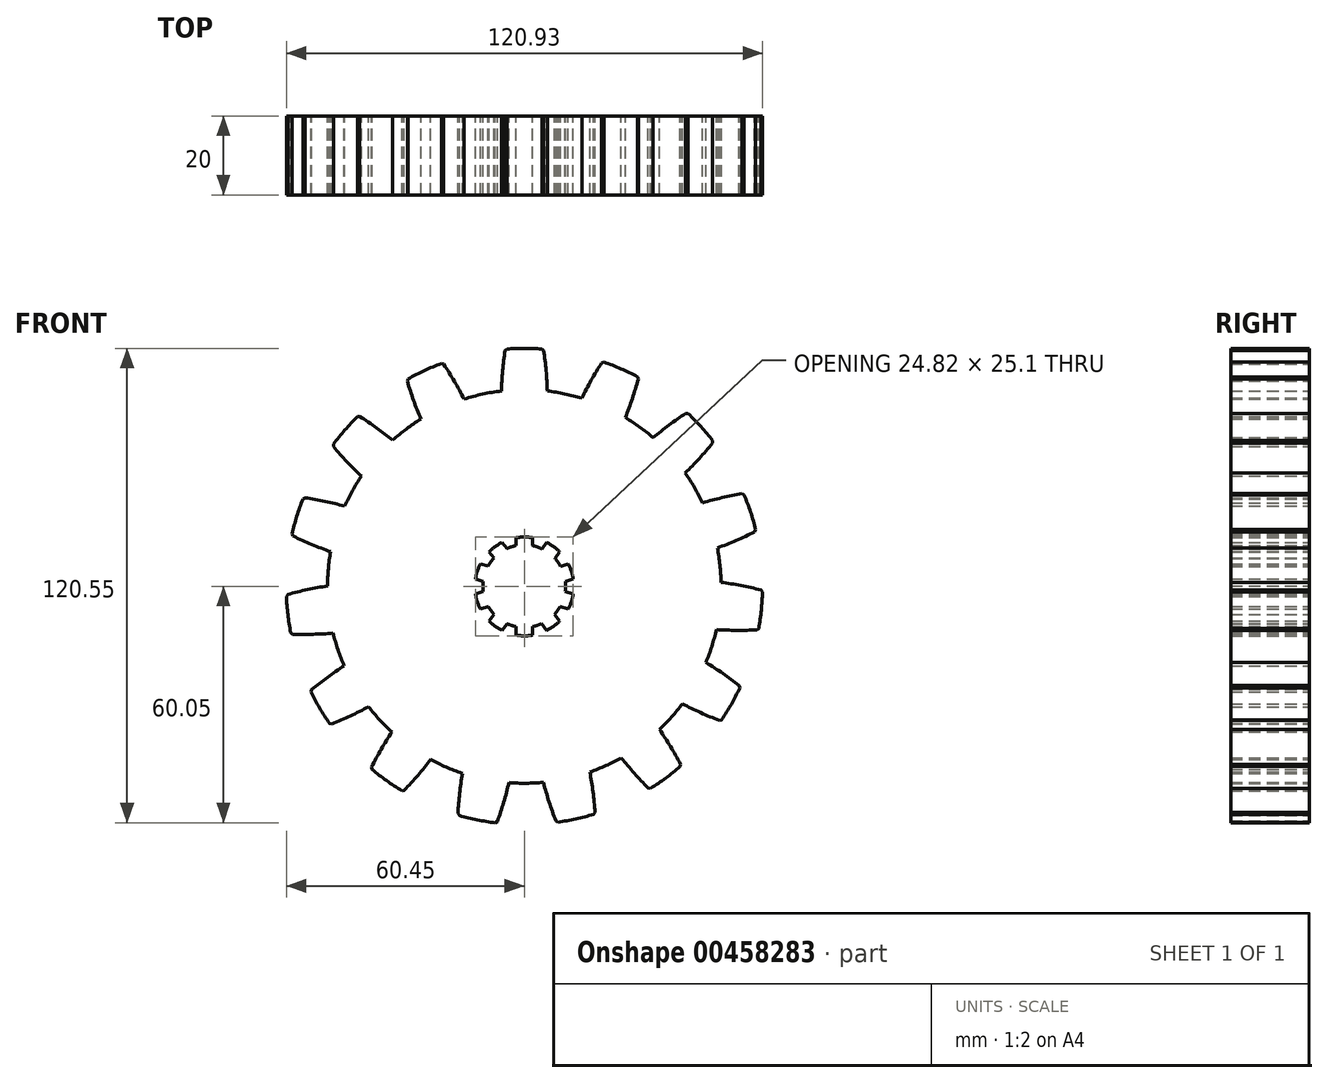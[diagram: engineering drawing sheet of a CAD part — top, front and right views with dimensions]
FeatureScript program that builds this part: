
annotation { "Feature Type Name" : "Feature", "Feature Type Description" : "" }
export const myFeature = defineFeature(function(context is Context, id is Id, definition is map)
    precondition{}
    {
        {
            var Q0;
            Q0=qCreatedBy(makeId("Front.planeOp"),FACE);
            var sketch = newSketch(context, id + "F0", { "sketchPlane" : qUnion([Q0])});
            skLineSegment(sketch, "E0.bottom", {"start": v(-2.05, 0) * mm, "end": v(2.05, 0) * mm});
            skLineSegment(sketch, "E0.left", {"start": v(-2.05, 0) * mm, "end": v(-2.05, 12.38) * mm});
            skLineSegment(sketch, "E0.right", {"start": v(2.05, 0) * mm, "end": v(2.05, 12.38) * mm});
            skArc(sketch, "E1", {"start": v(-5.62, 11.22) * mm, "mid": v(-7.38, 10.15) * mm, "end": v(-8.94, 8.81) * mm});
            skPoint(sketch, "E2", {"position": v(2.05, 12.38) * mm});
            skPoint(sketch, "E3", {"position": v(-2.05, 12.38) * mm});
            skLineSegment(sketch, "E4", {"start": v(-2.06, 12.38) * mm, "end": v(-2.05, 12.38) * mm, "construction": true});
            skLineSegment(sketch, "E5.1.0", {"start": v(1.66, 1.2) * mm, "end": v(-5.62, 11.22) * mm});
            skLineSegment(sketch, "E5.1.1", {"start": v(-1.66, -1.2) * mm, "end": v(-8.94, 8.81) * mm});
            skLineSegment(sketch, "E5.1.2", {"start": v(-1.66, -1.2) * mm, "end": v(1.66, 1.2) * mm});
            skLineSegment(sketch, "E5.2.0", {"start": v(0.63, 1.95) * mm, "end": v(-11.14, 5.78) * mm});
            skLineSegment(sketch, "E5.2.1", {"start": v(-0.63, -1.95) * mm, "end": v(-12.4, 1.88) * mm});
            skLineSegment(sketch, "E5.2.2", {"start": v(-0.63, -1.95) * mm, "end": v(0.63, 1.95) * mm});
            skLineSegment(sketch, "E5.3.0", {"start": v(-0.63, 1.95) * mm, "end": v(-12.4, -1.88) * mm});
            skLineSegment(sketch, "E5.3.1", {"start": v(0.63, -1.95) * mm, "end": v(-11.14, -5.78) * mm});
            skLineSegment(sketch, "E5.3.2", {"start": v(0.63, -1.95) * mm, "end": v(-0.63, 1.95) * mm});
            skLineSegment(sketch, "E5.4.0", {"start": v(-1.66, 1.2) * mm, "end": v(-8.94, -8.81) * mm});
            skLineSegment(sketch, "E5.4.1", {"start": v(1.66, -1.2) * mm, "end": v(-5.62, -11.22) * mm});
            skLineSegment(sketch, "E5.4.2", {"start": v(1.66, -1.2) * mm, "end": v(-1.66, 1.2) * mm});
            skLineSegment(sketch, "E5.5.0", {"start": v(-2.05, 0) * mm, "end": v(-2.05, -12.38) * mm});
            skLineSegment(sketch, "E5.5.1", {"start": v(2.05, 0) * mm, "end": v(2.05, -12.38) * mm});
            skLineSegment(sketch, "E5.5.2", {"start": v(2.05, 0) * mm, "end": v(-2.05, 0) * mm});
            skLineSegment(sketch, "E5.6.0", {"start": v(-1.66, -1.2) * mm, "end": v(5.62, -11.22) * mm});
            skLineSegment(sketch, "E5.6.1", {"start": v(1.66, 1.2) * mm, "end": v(8.94, -8.81) * mm});
            skLineSegment(sketch, "E5.6.2", {"start": v(1.66, 1.2) * mm, "end": v(-1.66, -1.2) * mm});
            skLineSegment(sketch, "E5.7.0", {"start": v(-0.63, -1.95) * mm, "end": v(11.14, -5.78) * mm});
            skLineSegment(sketch, "E5.7.1", {"start": v(0.63, 1.95) * mm, "end": v(12.4, -1.88) * mm});
            skLineSegment(sketch, "E5.7.2", {"start": v(0.63, 1.95) * mm, "end": v(-0.63, -1.95) * mm});
            skLineSegment(sketch, "E5.8.0", {"start": v(0.63, -1.95) * mm, "end": v(12.4, 1.88) * mm});
            skLineSegment(sketch, "E5.8.1", {"start": v(-0.63, 1.95) * mm, "end": v(11.14, 5.78) * mm});
            skLineSegment(sketch, "E5.8.2", {"start": v(-0.63, 1.95) * mm, "end": v(0.63, -1.95) * mm});
            skLineSegment(sketch, "E5.9.0", {"start": v(1.66, -1.2) * mm, "end": v(8.94, 8.81) * mm});
            skLineSegment(sketch, "E5.9.1", {"start": v(-1.66, 1.2) * mm, "end": v(5.62, 11.22) * mm});
            skLineSegment(sketch, "E5.9.2", {"start": v(-1.66, 1.2) * mm, "end": v(1.66, -1.2) * mm});
            skArc(sketch, "E6.trimOffspring", {"start": v(-11.14, 5.78) * mm, "mid": v(-11.94, 3.88) * mm, "end": v(-12.4, 1.88) * mm});
            skArc(sketch, "E7.trimOffspring", {"start": v(-12.4, -1.88) * mm, "mid": v(-11.94, -3.88) * mm, "end": v(-11.14, -5.78) * mm});
            skArc(sketch, "E8.trimOffspring", {"start": v(-8.94, -8.81) * mm, "mid": v(-7.38, -10.15) * mm, "end": v(-5.62, -11.22) * mm});
            skArc(sketch, "E9.trimOffspring", {"start": v(-2.05, -12.38) * mm, "mid": v(0, -12.55) * mm, "end": v(2.05, -12.38) * mm});
            skArc(sketch, "E10.trimOffspring", {"start": v(5.62, -11.22) * mm, "mid": v(7.38, -10.15) * mm, "end": v(8.94, -8.81) * mm});
            skArc(sketch, "E11.trimOffspring", {"start": v(11.14, -5.78) * mm, "mid": v(11.94, -3.88) * mm, "end": v(12.4, -1.88) * mm});
            skArc(sketch, "E12.trimOffspring", {"start": v(12.4, 1.88) * mm, "mid": v(11.94, 3.88) * mm, "end": v(11.14, 5.78) * mm});
            skArc(sketch, "E13.trimOffspring", {"start": v(8.94, 8.81) * mm, "mid": v(7.38, 10.15) * mm, "end": v(5.62, 11.22) * mm});
            skArc(sketch, "E14.trimOffspring", {"start": v(2.05, 12.38) * mm, "mid": v(0, 12.55) * mm, "end": v(-2.06, 12.38) * mm});
            skCircle(sketch, "E15", {"center": v(-0.03, 0.08) * mm, "radius": 10.5 * mm});
            skSolve(sketch);
        }
        {
            var Q0;
            Q0=qCreatedBy(makeId("Front.planeOp"),FACE);
            var sketch = newSketch(context, id + "F1", { "sketchPlane" : qUnion([Q0])});
            skCircle(sketch, "E16", {"center": v(0, 0) * mm, "radius": 50 * mm});
            skLineSegment(sketch, "E17", {"start": v(0, 50) * mm, "end": v(-29, 50) * mm, "construction": true});
            skLineSegment(sketch, "E18", {"start": v(-29, 50) * mm, "end": v(-29, 46.5) * mm, "construction": true});
            skLineSegment(sketch, "E19", {"start": v(-29, 46.5) * mm, "end": v(0, 46.5) * mm, "construction": true});
            skLineSegment(sketch, "E20", {"start": v(0, 46.5) * mm, "end": v(84.1, 46.5) * mm, "construction": true});
            skArc(sketch, "E21", {"start": v(-4.83, 60.3) * mm, "mid": v(-5.5, 55) * mm, "end": v(-5.84, 49.66) * mm});
            skArc(sketch, "E22.MirrorC", {"start": v(4.83, 60.3) * mm, "mid": v(5.5, 55) * mm, "end": v(5.84, 49.66) * mm});
            skArc(sketch, "E23", {"start": v(4.83, 60.3) * mm, "mid": v(0, 60.5) * mm, "end": v(-4.83, 60.3) * mm});
            skArc(sketch, "E24.1.0", {"start": v(29.06, 53.07) * mm, "mid": v(24.54, 55.3) * mm, "end": v(19.85, 57.15) * mm});
            skArc(sketch, "E24.1.1", {"start": v(29.06, 53.07) * mm, "mid": v(27.5, 47.94) * mm, "end": v(25.66, 42.92) * mm});
            skArc(sketch, "E24.1.2", {"start": v(19.85, 57.15) * mm, "mid": v(17.09, 52.56) * mm, "end": v(14.6, 47.82) * mm});
            skArc(sketch, "E24.2.0", {"start": v(48.08, 36.72) * mm, "mid": v(44.86, 40.6) * mm, "end": v(41.32, 44.19) * mm});
            skArc(sketch, "E24.2.1", {"start": v(48.08, 36.72) * mm, "mid": v(44.59, 32.66) * mm, "end": v(40.86, 28.82) * mm});
            skArc(sketch, "E24.2.2", {"start": v(41.32, 44.19) * mm, "mid": v(36.94, 41.11) * mm, "end": v(32.75, 37.79) * mm});
            skArc(sketch, "E24.3.0", {"start": v(58.84, 14.06) * mm, "mid": v(57.47, 18.91) * mm, "end": v(55.7, 23.63) * mm});
            skArc(sketch, "E24.3.1", {"start": v(58.84, 14.06) * mm, "mid": v(54, 11.77) * mm, "end": v(49.04, 9.77) * mm});
            skArc(sketch, "E24.3.2", {"start": v(55.7, 23.63) * mm, "mid": v(50.44, 22.6) * mm, "end": v(45.26, 21.26) * mm});
            skArc(sketch, "E24.4.0", {"start": v(59.49, -11.02) * mm, "mid": v(60.2, -6.02) * mm, "end": v(60.5, -1) * mm});
            skArc(sketch, "E24.4.1", {"start": v(59.49, -11.02) * mm, "mid": v(54.14, -11.15) * mm, "end": v(48.78, -10.96) * mm});
            skArc(sketch, "E24.4.2", {"start": v(60.5, -1) * mm, "mid": v(55.27, 0.2) * mm, "end": v(49.99, 1.07) * mm});
            skArc(sketch, "E24.5.0", {"start": v(49.9, -34.2) * mm, "mid": v(52.58, -29.92) * mm, "end": v(54.9, -25.44) * mm});
            skArc(sketch, "E24.5.1", {"start": v(49.9, -34.2) * mm, "mid": v(44.96, -32.14) * mm, "end": v(40.15, -29.8) * mm});
            skArc(sketch, "E24.5.2", {"start": v(54.9, -25.44) * mm, "mid": v(50.6, -22.24) * mm, "end": v(46.13, -19.3) * mm});
            skArc(sketch, "E24.6.0", {"start": v(31.75, -51.5) * mm, "mid": v(35.93, -48.68) * mm, "end": v(39.85, -45.52) * mm});
            skArc(sketch, "E24.6.1", {"start": v(31.75, -51.5) * mm, "mid": v(28.06, -47.62) * mm, "end": v(24.6, -43.52) * mm});
            skArc(sketch, "E24.6.2", {"start": v(39.85, -45.52) * mm, "mid": v(37.23, -40.85) * mm, "end": v(34.34, -36.34) * mm});
            skArc(sketch, "E24.7.0", {"start": v(8.13, -59.95) * mm, "mid": v(13.1, -59.07) * mm, "end": v(17.97, -57.77) * mm});
            skArc(sketch, "E24.7.1", {"start": v(8.13, -59.95) * mm, "mid": v(6.33, -54.9) * mm, "end": v(4.84, -49.77) * mm});
            skArc(sketch, "E24.7.2", {"start": v(17.97, -57.77) * mm, "mid": v(17.46, -52.44) * mm, "end": v(16.64, -47.15) * mm});
            skArc(sketch, "E24.8.0", {"start": v(-16.88, -58.1) * mm, "mid": v(-11.99, -59.3) * mm, "end": v(-7, -60.1) * mm});
            skArc(sketch, "E24.8.1", {"start": v(-16.88, -58.1) * mm, "mid": v(-16.48, -52.76) * mm, "end": v(-15.76, -47.45) * mm});
            skArc(sketch, "E24.8.2", {"start": v(-7, -60.1) * mm, "mid": v(-5.3, -55.02) * mm, "end": v(-3.9, -49.85) * mm});
            skArc(sketch, "E24.9.0", {"start": v(-39, -46.26) * mm, "mid": v(-35, -49.34) * mm, "end": v(-30.78, -52.09) * mm});
            skArc(sketch, "E24.9.1", {"start": v(-39, -46.26) * mm, "mid": v(-36.46, -41.54) * mm, "end": v(-33.65, -36.98) * mm});
            skArc(sketch, "E24.9.2", {"start": v(-30.78, -52.09) * mm, "mid": v(-27.16, -48.14) * mm, "end": v(-23.8, -43.98) * mm});
            skArc(sketch, "E24.10.0", {"start": v(-54.4, -26.46) * mm, "mid": v(-52.01, -30.9) * mm, "end": v(-49.26, -35.12) * mm});
            skArc(sketch, "E24.10.1", {"start": v(-54.4, -26.46) * mm, "mid": v(-50.18, -23.18) * mm, "end": v(-45.76, -20.15) * mm});
            skArc(sketch, "E24.10.2", {"start": v(-49.26, -35.12) * mm, "mid": v(-44.35, -32.98) * mm, "end": v(-39.58, -30.55) * mm});
            skArc(sketch, "E24.11.0", {"start": v(-60.46, -2.12) * mm, "mid": v(-60.08, -7.15) * mm, "end": v(-59.27, -12.13) * mm});
            skArc(sketch, "E24.11.1", {"start": v(-60.46, -2.12) * mm, "mid": v(-55.26, -0.84) * mm, "end": v(-50, 0.14) * mm});
            skArc(sketch, "E24.11.2", {"start": v(-59.27, -12.13) * mm, "mid": v(-53.92, -12.16) * mm, "end": v(-48.57, -11.87) * mm});
            skArc(sketch, "E24.12.0", {"start": v(-56.13, 22.58) * mm, "mid": v(-57.81, 17.83) * mm, "end": v(-59.1, 12.96) * mm});
            skArc(sketch, "E24.12.1", {"start": v(-56.13, 22.58) * mm, "mid": v(-50.85, 21.65) * mm, "end": v(-45.65, 20.4) * mm});
            skArc(sketch, "E24.12.2", {"start": v(-59.1, 12.96) * mm, "mid": v(-54.21, 10.76) * mm, "end": v(-49.21, 8.85) * mm});
            skArc(sketch, "E24.13.0", {"start": v(-42.14, 43.4) * mm, "mid": v(-45.61, 39.75) * mm, "end": v(-48.76, 35.81) * mm});
            skArc(sketch, "E24.13.1", {"start": v(-42.14, 43.4) * mm, "mid": v(-37.7, 40.42) * mm, "end": v(-33.45, 37.17) * mm});
            skArc(sketch, "E24.13.2", {"start": v(-48.76, 35.81) * mm, "mid": v(-45.2, 31.82) * mm, "end": v(-41.39, 28.05) * mm});
            skArc(sketch, "E24.14.0", {"start": v(-20.71, 56.79) * mm, "mid": v(-25.37, 54.85) * mm, "end": v(-29.84, 52.53) * mm});
            skArc(sketch, "E24.14.1", {"start": v(-20.71, 56.79) * mm, "mid": v(-17.87, 52.25) * mm, "end": v(-15.3, 47.55) * mm});
            skArc(sketch, "E24.14.2", {"start": v(-29.84, 52.53) * mm, "mid": v(-28.2, 47.43) * mm, "end": v(-26.25, 42.44) * mm});
            skPoint(sketch, "E24.center", {"position": v(0.2, 0.02) * mm});
            skLineSegment(sketch, "E24.anchor1", {"start": v(0.2, 0.02) * mm, "end": v(-4.83, 60.3) * mm, "construction": true});
            skLineSegment(sketch, "E24.anchor2", {"start": v(0.2, 0.02) * mm, "end": v(-29.84, 52.53) * mm, "construction": true});
            skSolve(sketch);
        }
        {
            var Q0;
            Q0 = qSketchRegion(id + "F1", true);
            extrude(context, id + "F2", {"entities" : qUnion([Q0]), "depth" : 20 * mm, "offsetDistance" : 25 * mm});
        }
        {
            var Q0;
            Q0 = qSketchRegion(id + "F0", true);
            var Q1;
            Q1=makeQuery(id+"F2.opExtrude","CAP_FACE",FACE,{"disambiguationData":[OSD([sQuery(id+"F1.wireOp",EDGE,"E16"),sQuery(id+"F1.wireOp",EDGE,"E21"),sQuery(id+"F1.wireOp",EDGE,"E22.MirrorC"),sQuery(id+"F1.wireOp",EDGE,"E23"),sQuery(id+"F1.wireOp",EDGE,"E24.1.0"),sQuery(id+"F1.wireOp",EDGE,"E24.1.1"),sQuery(id+"F1.wireOp",EDGE,"E24.1.2"),sQuery(id+"F1.wireOp",EDGE,"E24.2.0"),sQuery(id+"F1.wireOp",EDGE,"E24.2.1"),sQuery(id+"F1.wireOp",EDGE,"E24.2.2"),sQuery(id+"F1.wireOp",EDGE,"E24.3.0"),sQuery(id+"F1.wireOp",EDGE,"E24.3.1"),sQuery(id+"F1.wireOp",EDGE,"E24.3.2"),sQuery(id+"F1.wireOp",EDGE,"E24.4.0"),sQuery(id+"F1.wireOp",EDGE,"E24.4.1"),sQuery(id+"F1.wireOp",EDGE,"E24.4.2"),sQuery(id+"F1.wireOp",EDGE,"E24.5.0"),sQuery(id+"F1.wireOp",EDGE,"E24.5.1"),sQuery(id+"F1.wireOp",EDGE,"E24.5.2"),sQuery(id+"F1.wireOp",EDGE,"E24.6.0"),sQuery(id+"F1.wireOp",EDGE,"E24.6.1"),sQuery(id+"F1.wireOp",EDGE,"E24.6.2"),sQuery(id+"F1.wireOp",EDGE,"E24.7.0"),sQuery(id+"F1.wireOp",EDGE,"E24.7.1"),sQuery(id+"F1.wireOp",EDGE,"E24.7.2"),sQuery(id+"F1.wireOp",EDGE,"E24.8.0"),sQuery(id+"F1.wireOp",EDGE,"E24.8.1"),sQuery(id+"F1.wireOp",EDGE,"E24.8.2"),sQuery(id+"F1.wireOp",EDGE,"E24.9.0"),sQuery(id+"F1.wireOp",EDGE,"E24.9.1"),sQuery(id+"F1.wireOp",EDGE,"E24.9.2"),sQuery(id+"F1.wireOp",EDGE,"E24.10.0"),sQuery(id+"F1.wireOp",EDGE,"E24.10.1"),sQuery(id+"F1.wireOp",EDGE,"E24.10.2"),sQuery(id+"F1.wireOp",EDGE,"E24.11.0"),sQuery(id+"F1.wireOp",EDGE,"E24.11.1"),sQuery(id+"F1.wireOp",EDGE,"E24.11.2"),sQuery(id+"F1.wireOp",EDGE,"E24.12.0"),sQuery(id+"F1.wireOp",EDGE,"E24.12.1"),sQuery(id+"F1.wireOp",EDGE,"E24.12.2"),sQuery(id+"F1.wireOp",EDGE,"E24.13.0"),sQuery(id+"F1.wireOp",EDGE,"E24.13.1"),sQuery(id+"F1.wireOp",EDGE,"E24.13.2"),sQuery(id+"F1.wireOp",EDGE,"E24.14.0"),sQuery(id+"F1.wireOp",EDGE,"E24.14.1"),sQuery(id+"F1.wireOp",EDGE,"E24.14.2")])],"isStart":false});
            extrude(context, id + "F3", {"entities" : qUnion([Q0]), "operationType" : NewBodyOperationType.REMOVE, "endBound" : BoundingType.UP_TO_SURFACE, "endBoundEntityFace" : qUnion([Q1]), "depth" : 25 * mm});
        }
        {
            var Q0;
            {var subQ13=sQuery(id+"F0.wireOp",EDGE,"E5.2.0");var subQ14=sQuery(id+"F0.wireOp",EDGE,"E0.left");var subQ15=makeQuery(id+"F0.imprint","INTERSECT",VERTEX,{"derivedFrom":[subQ14,subQ13]});Q0=makeQuery(id+"F3.boolean.opBoolean","SPLIT",FACE,{"disambiguationData":[TD([makeQuery(id+"F3.opExtrude","SWEPT_FACE",FACE,{"disambiguationData":[OSD([subQ14]),TDD([makeQuery(id+"F0.imprint","IMPRINT",EDGE,{"disambiguationData":[TD([[subQ15,-1.0]])],"derivedFrom":subQ14})])]})])],"derivedFrom":makeQuery(id+"F2.opExtrude","CAP_FACE",FACE,{"disambiguationData":[OSD([sQuery(id+"F1.wireOp",EDGE,"E16"),sQuery(id+"F1.wireOp",EDGE,"E21"),sQuery(id+"F1.wireOp",EDGE,"E22.MirrorC"),sQuery(id+"F1.wireOp",EDGE,"E23"),sQuery(id+"F1.wireOp",EDGE,"E24.1.0"),sQuery(id+"F1.wireOp",EDGE,"E24.1.1"),sQuery(id+"F1.wireOp",EDGE,"E24.1.2"),sQuery(id+"F1.wireOp",EDGE,"E24.2.0"),sQuery(id+"F1.wireOp",EDGE,"E24.2.1"),sQuery(id+"F1.wireOp",EDGE,"E24.2.2"),sQuery(id+"F1.wireOp",EDGE,"E24.3.0"),sQuery(id+"F1.wireOp",EDGE,"E24.3.1"),sQuery(id+"F1.wireOp",EDGE,"E24.3.2"),sQuery(id+"F1.wireOp",EDGE,"E24.4.0"),sQuery(id+"F1.wireOp",EDGE,"E24.4.1"),sQuery(id+"F1.wireOp",EDGE,"E24.4.2"),sQuery(id+"F1.wireOp",EDGE,"E24.5.0"),sQuery(id+"F1.wireOp",EDGE,"E24.5.1"),sQuery(id+"F1.wireOp",EDGE,"E24.5.2"),sQuery(id+"F1.wireOp",EDGE,"E24.6.0"),sQuery(id+"F1.wireOp",EDGE,"E24.6.1"),sQuery(id+"F1.wireOp",EDGE,"E24.6.2"),sQuery(id+"F1.wireOp",EDGE,"E24.7.0"),sQuery(id+"F1.wireOp",EDGE,"E24.7.1"),sQuery(id+"F1.wireOp",EDGE,"E24.7.2"),sQuery(id+"F1.wireOp",EDGE,"E24.8.0"),sQuery(id+"F1.wireOp",EDGE,"E24.8.1"),sQuery(id+"F1.wireOp",EDGE,"E24.8.2"),sQuery(id+"F1.wireOp",EDGE,"E24.9.0"),sQuery(id+"F1.wireOp",EDGE,"E24.9.1"),sQuery(id+"F1.wireOp",EDGE,"E24.9.2"),sQuery(id+"F1.wireOp",EDGE,"E24.10.0"),sQuery(id+"F1.wireOp",EDGE,"E24.10.1"),sQuery(id+"F1.wireOp",EDGE,"E24.10.2"),sQuery(id+"F1.wireOp",EDGE,"E24.11.0"),sQuery(id+"F1.wireOp",EDGE,"E24.11.1"),sQuery(id+"F1.wireOp",EDGE,"E24.11.2"),sQuery(id+"F1.wireOp",EDGE,"E24.12.0"),sQuery(id+"F1.wireOp",EDGE,"E24.12.1"),sQuery(id+"F1.wireOp",EDGE,"E24.12.2"),sQuery(id+"F1.wireOp",EDGE,"E24.13.0"),sQuery(id+"F1.wireOp",EDGE,"E24.13.1"),sQuery(id+"F1.wireOp",EDGE,"E24.13.2"),sQuery(id+"F1.wireOp",EDGE,"E24.14.0"),sQuery(id+"F1.wireOp",EDGE,"E24.14.1"),sQuery(id+"F1.wireOp",EDGE,"E24.14.2")])],"isStart":false})});}
            var Q1;
            {var subQ9=sQuery(id+"F1.wireOp",EDGE,"E24.14.2");var subQ18=sQuery(id+"F1.wireOp",EDGE,"E24.14.1");var subQ27=sQuery(id+"F1.wireOp",EDGE,"E24.14.0");var subQ29=sQuery(id+"F1.wireOp",EDGE,"E24.13.2");var subQ31=sQuery(id+"F1.wireOp",EDGE,"E24.13.1");var subQ33=sQuery(id+"F1.wireOp",EDGE,"E24.13.0");var subQ35=sQuery(id+"F1.wireOp",EDGE,"E24.12.2");var subQ37=sQuery(id+"F1.wireOp",EDGE,"E24.12.1");var subQ39=sQuery(id+"F1.wireOp",EDGE,"E24.12.0");var subQ41=sQuery(id+"F1.wireOp",EDGE,"E24.11.2");var subQ43=sQuery(id+"F1.wireOp",EDGE,"E24.11.1");var subQ45=sQuery(id+"F1.wireOp",EDGE,"E24.11.0");var subQ46=sQuery(id+"F1.wireOp",EDGE,"E24.10.2");var subQ47=sQuery(id+"F1.wireOp",EDGE,"E24.10.1");var subQ48=sQuery(id+"F1.wireOp",EDGE,"E24.1.2");var subQ49=sQuery(id+"F1.wireOp",EDGE,"E24.2.1");var subQ50=sQuery(id+"F1.wireOp",EDGE,"E24.1.1");var subQ51=sQuery(id+"F1.wireOp",EDGE,"E24.1.0");var subQ52=sQuery(id+"F1.wireOp",EDGE,"E23");var subQ53=sQuery(id+"F1.wireOp",EDGE,"E22.MirrorC");var subQ55=sQuery(id+"F1.wireOp",EDGE,"E21");var subQ56=sQuery(id+"F1.wireOp",EDGE,"E24.4.1");var subQ57=sQuery(id+"F1.wireOp",EDGE,"E16");var subQ58=sQuery(id+"F1.wireOp",EDGE,"E24.5.2");var subQ59=sQuery(id+"F1.wireOp",EDGE,"E24.5.1");var subQ60=sQuery(id+"F1.wireOp",EDGE,"E24.6.2");var subQ61=sQuery(id+"F1.wireOp",EDGE,"E24.6.1");var subQ62=sQuery(id+"F1.wireOp",EDGE,"E24.7.2");var subQ63=sQuery(id+"F1.wireOp",EDGE,"E24.7.1");var subQ64=sQuery(id+"F1.wireOp",EDGE,"E24.8.2");var subQ65=sQuery(id+"F1.wireOp",EDGE,"E24.8.1");var subQ66=sQuery(id+"F1.wireOp",EDGE,"E24.9.2");var subQ67=sQuery(id+"F1.wireOp",EDGE,"E24.2.2");var subQ68=sQuery(id+"F1.wireOp",EDGE,"E24.3.2");var subQ69=sQuery(id+"F1.wireOp",EDGE,"E24.3.0");var subQ70=sQuery(id+"F1.wireOp",EDGE,"E24.2.0");var subQ71=sQuery(id+"F1.wireOp",EDGE,"E24.3.1");var subQ72=sQuery(id+"F1.wireOp",EDGE,"E24.4.2");var subQ73=sQuery(id+"F1.wireOp",EDGE,"E24.10.0");var subQ74=sQuery(id+"F1.wireOp",EDGE,"E24.9.1");var subQ79=sQuery(id+"F1.wireOp",EDGE,"E24.5.0");var subQ80=sQuery(id+"F1.wireOp",EDGE,"E24.4.0");var subQ87=sQuery(id+"F1.wireOp",EDGE,"E24.7.0");var subQ88=sQuery(id+"F1.wireOp",EDGE,"E24.6.0");var subQ95=sQuery(id+"F1.wireOp",EDGE,"E24.9.0");var subQ96=sQuery(id+"F1.wireOp",EDGE,"E24.8.0");Q1=makeQuery(id+"F3.boolean.opBoolean","SPLIT",FACE,{"disambiguationData":[TD([makeQuery(id+"F2.opExtrude","SWEPT_FACE",FACE,{"disambiguationData":[OSD([subQ55])]})])],"derivedFrom":makeQuery(id+"F2.opExtrude","CAP_FACE",FACE,{"disambiguationData":[OSD([subQ57,subQ55,subQ53,subQ52,subQ51,subQ50,subQ48,subQ70,subQ49,subQ67,subQ69,subQ71,subQ68,subQ80,subQ56,subQ72,subQ79,subQ59,subQ58,subQ88,subQ61,subQ60,subQ87,subQ63,subQ62,subQ96,subQ65,subQ64,subQ95,subQ74,subQ66,subQ73,subQ47,subQ46,subQ45,subQ43,subQ41,subQ39,subQ37,subQ35,subQ33,subQ31,subQ29,subQ27,subQ18,subQ9])],"isStart":true})});}
            extrude(context, id + "F4", {"entities" : qUnion([Q0]), "operationType" : NewBodyOperationType.REMOVE, "oppositeDirection" : true, "endBoundEntityFace" : qUnion([Q1]), "depth" : 20 * mm});
        }
        {
            var Q0;
            Q0=makeQuery(id+"F2.opExtrude","SWEPT_EDGE",EDGE,{"disambiguationData":[OSD([sQuery(id+"F1.wireOp",EDGE,"E24.14.0"),sQuery(id+"F1.wireOp",EDGE,"E24.14.2")])]});
            var Q1;
            Q1=makeQuery(id+"F2.opExtrude","SWEPT_EDGE",EDGE,{"disambiguationData":[OSD([sQuery(id+"F1.wireOp",EDGE,"E24.14.0"),sQuery(id+"F1.wireOp",EDGE,"E24.14.1")])]});
            var Q2;
            Q2=makeQuery(id+"F2.opExtrude","SWEPT_EDGE",EDGE,{"disambiguationData":[OSD([sQuery(id+"F1.wireOp",EDGE,"E21"),sQuery(id+"F1.wireOp",EDGE,"E23")])]});
            var Q3;
            Q3=makeQuery(id+"F2.opExtrude","SWEPT_EDGE",EDGE,{"disambiguationData":[OSD([sQuery(id+"F1.wireOp",EDGE,"E22.MirrorC"),sQuery(id+"F1.wireOp",EDGE,"E23")])]});
            var Q4;
            Q4=makeQuery(id+"F2.opExtrude","SWEPT_EDGE",EDGE,{"disambiguationData":[OSD([sQuery(id+"F1.wireOp",EDGE,"E24.1.0"),sQuery(id+"F1.wireOp",EDGE,"E24.1.2")])]});
            var Q5;
            Q5=makeQuery(id+"F2.opExtrude","SWEPT_EDGE",EDGE,{"disambiguationData":[OSD([sQuery(id+"F1.wireOp",EDGE,"E24.1.0"),sQuery(id+"F1.wireOp",EDGE,"E24.1.1")])]});
            var Q6;
            Q6=makeQuery(id+"F2.opExtrude","SWEPT_EDGE",EDGE,{"disambiguationData":[OSD([sQuery(id+"F1.wireOp",EDGE,"E24.2.0"),sQuery(id+"F1.wireOp",EDGE,"E24.2.2")])]});
            var Q7;
            Q7=makeQuery(id+"F2.opExtrude","SWEPT_EDGE",EDGE,{"disambiguationData":[OSD([sQuery(id+"F1.wireOp",EDGE,"E24.2.0"),sQuery(id+"F1.wireOp",EDGE,"E24.2.1")])]});
            var Q8;
            Q8=makeQuery(id+"F2.opExtrude","SWEPT_EDGE",EDGE,{"disambiguationData":[OSD([sQuery(id+"F1.wireOp",EDGE,"E24.3.0"),sQuery(id+"F1.wireOp",EDGE,"E24.3.2")])]});
            var Q9;
            Q9=makeQuery(id+"F2.opExtrude","SWEPT_EDGE",EDGE,{"disambiguationData":[OSD([sQuery(id+"F1.wireOp",EDGE,"E24.3.0"),sQuery(id+"F1.wireOp",EDGE,"E24.3.1")])]});
            var Q10;
            Q10=makeQuery(id+"F2.opExtrude","SWEPT_EDGE",EDGE,{"disambiguationData":[OSD([sQuery(id+"F1.wireOp",EDGE,"E24.4.0"),sQuery(id+"F1.wireOp",EDGE,"E24.4.2")])]});
            var Q11;
            Q11=makeQuery(id+"F2.opExtrude","SWEPT_EDGE",EDGE,{"disambiguationData":[OSD([sQuery(id+"F1.wireOp",EDGE,"E24.4.0"),sQuery(id+"F1.wireOp",EDGE,"E24.4.1")])]});
            var Q12;
            Q12=makeQuery(id+"F2.opExtrude","SWEPT_EDGE",EDGE,{"disambiguationData":[OSD([sQuery(id+"F1.wireOp",EDGE,"E24.5.0"),sQuery(id+"F1.wireOp",EDGE,"E24.5.2")])]});
            var Q13;
            Q13=makeQuery(id+"F2.opExtrude","SWEPT_EDGE",EDGE,{"disambiguationData":[OSD([sQuery(id+"F1.wireOp",EDGE,"E24.5.0"),sQuery(id+"F1.wireOp",EDGE,"E24.5.1")])]});
            var Q14;
            Q14=makeQuery(id+"F2.opExtrude","SWEPT_EDGE",EDGE,{"disambiguationData":[OSD([sQuery(id+"F1.wireOp",EDGE,"E24.6.0"),sQuery(id+"F1.wireOp",EDGE,"E24.6.2")])]});
            var Q15;
            Q15=makeQuery(id+"F2.opExtrude","SWEPT_EDGE",EDGE,{"disambiguationData":[OSD([sQuery(id+"F1.wireOp",EDGE,"E24.6.0"),sQuery(id+"F1.wireOp",EDGE,"E24.6.1")])]});
            var Q16;
            Q16=makeQuery(id+"F2.opExtrude","SWEPT_EDGE",EDGE,{"disambiguationData":[OSD([sQuery(id+"F1.wireOp",EDGE,"E24.7.0"),sQuery(id+"F1.wireOp",EDGE,"E24.7.2")])]});
            var Q17;
            Q17=makeQuery(id+"F2.opExtrude","SWEPT_EDGE",EDGE,{"disambiguationData":[OSD([sQuery(id+"F1.wireOp",EDGE,"E24.7.0"),sQuery(id+"F1.wireOp",EDGE,"E24.7.1")])]});
            var Q18;
            Q18=makeQuery(id+"F2.opExtrude","SWEPT_EDGE",EDGE,{"disambiguationData":[OSD([sQuery(id+"F1.wireOp",EDGE,"E24.9.0"),sQuery(id+"F1.wireOp",EDGE,"E24.9.2")])]});
            var Q19;
            Q19=makeQuery(id+"F2.opExtrude","SWEPT_EDGE",EDGE,{"disambiguationData":[OSD([sQuery(id+"F1.wireOp",EDGE,"E24.9.0"),sQuery(id+"F1.wireOp",EDGE,"E24.9.1")])]});
            var Q20;
            Q20=makeQuery(id+"F2.opExtrude","SWEPT_EDGE",EDGE,{"disambiguationData":[OSD([sQuery(id+"F1.wireOp",EDGE,"E24.10.0"),sQuery(id+"F1.wireOp",EDGE,"E24.10.2")])]});
            var Q21;
            Q21=makeQuery(id+"F2.opExtrude","SWEPT_EDGE",EDGE,{"disambiguationData":[OSD([sQuery(id+"F1.wireOp",EDGE,"E24.10.0"),sQuery(id+"F1.wireOp",EDGE,"E24.10.1")])]});
            var Q22;
            Q22=makeQuery(id+"F2.opExtrude","SWEPT_EDGE",EDGE,{"disambiguationData":[OSD([sQuery(id+"F1.wireOp",EDGE,"E24.8.0"),sQuery(id+"F1.wireOp",EDGE,"E24.8.1")])]});
            var Q23;
            Q23=makeQuery(id+"F2.opExtrude","SWEPT_EDGE",EDGE,{"disambiguationData":[OSD([sQuery(id+"F1.wireOp",EDGE,"E24.8.0"),sQuery(id+"F1.wireOp",EDGE,"E24.8.2")])]});
            var Q24;
            Q24=makeQuery(id+"F2.opExtrude","SWEPT_EDGE",EDGE,{"disambiguationData":[OSD([sQuery(id+"F1.wireOp",EDGE,"E24.11.0"),sQuery(id+"F1.wireOp",EDGE,"E24.11.2")])]});
            var Q25;
            Q25=makeQuery(id+"F2.opExtrude","SWEPT_EDGE",EDGE,{"disambiguationData":[OSD([sQuery(id+"F1.wireOp",EDGE,"E24.11.0"),sQuery(id+"F1.wireOp",EDGE,"E24.11.1")])]});
            var Q26;
            Q26=makeQuery(id+"F2.opExtrude","SWEPT_EDGE",EDGE,{"disambiguationData":[OSD([sQuery(id+"F1.wireOp",EDGE,"E24.12.0"),sQuery(id+"F1.wireOp",EDGE,"E24.12.1")])]});
            var Q27;
            Q27=makeQuery(id+"F2.opExtrude","SWEPT_EDGE",EDGE,{"disambiguationData":[OSD([sQuery(id+"F1.wireOp",EDGE,"E24.12.0"),sQuery(id+"F1.wireOp",EDGE,"E24.12.2")])]});
            var Q28;
            Q28=makeQuery(id+"F2.opExtrude","SWEPT_EDGE",EDGE,{"disambiguationData":[OSD([sQuery(id+"F1.wireOp",EDGE,"E24.13.0"),sQuery(id+"F1.wireOp",EDGE,"E24.13.2")])]});
            var Q29;
            Q29=makeQuery(id+"F2.opExtrude","SWEPT_EDGE",EDGE,{"disambiguationData":[OSD([sQuery(id+"F1.wireOp",EDGE,"E24.13.0"),sQuery(id+"F1.wireOp",EDGE,"E24.13.1")])]});
            chamfer(context, id + "F5", {"entities" : qUnion([Q0, Q1, Q2, Q3, Q4, Q5, Q6, Q7, Q8, Q9, Q10, Q11, Q12, Q13, Q14, Q15, Q16, Q17, Q18, Q19, Q20, Q21, Q22, Q23, Q24, Q25, Q26, Q27, Q28, Q29]), "width" : .5 * mm, "tangentPropagation" : true});
        }
    });
